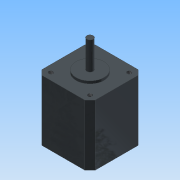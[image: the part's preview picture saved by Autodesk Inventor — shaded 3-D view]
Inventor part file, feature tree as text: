
AUTODESK INVENTOR PART (.ipt)
format: ipt  version: 2015 (Build 190159000, 159)  size: 144,384 bytes
history: native  units: mm
features: sketch x4, extrude x3, chamfer x3, hole x1, projected_geometry x1
ambient origin geometry x8: Origin, YZ Plane, XZ Plane, XY Plane, X Axis, Y Axis, Z Axis, Center Point
bodies: Solid1 (feature_tree)
feature tree (12):
  extrude  "Extrusion1"  Depth=42.0mm
  chamfer  "Chamfer1"  Distance=48.0mm
  chamfer  "Chamfer2"  Distance=2.0mm Angle=45.0deg
  chamfer  "Chamfer3"  Distance=2.0mm Angle=45.0deg
  extrude  "Extrusion2"  Depth=22.0mm
  extrude  "Extrusion3"  Depth=2.0mm
  hole  "Hole1"  [1 undecoded]
  sketch  "Sketch1"  dims[d0=42.0mm d1=42.0mm d2=48.0mm d3=0.0mm d4=4.0mm d5=2.0mm d6=45.0deg d7=4.0mm d8=2.0mm d9=45.0deg]
  sketch  "Sketch2"  dims[d10=4.0mm d11=2.0mm d12=45.0deg d13=22.0mm]
  sketch  "Sketch3"  dims[d14=2.0mm d15=0.0mm d16=5.0mm]
  sketch  "Sketch4"  dims[d17=22.0mm d18=0.0mm d19=31.0mm d20=31.0mm d21=3.242mm d22=6.0mm d23=4.0mm d24=2.0mm d25=90.0deg d26=4.0mm d27=20.594885mm]
  projected_geometry  "Projected Loop1"
note: 1 required parameter value undecoded (feature->parameter linkage not recoverable at this tier; creation-order binding heuristic only, values carry confidence <= 0.55)
